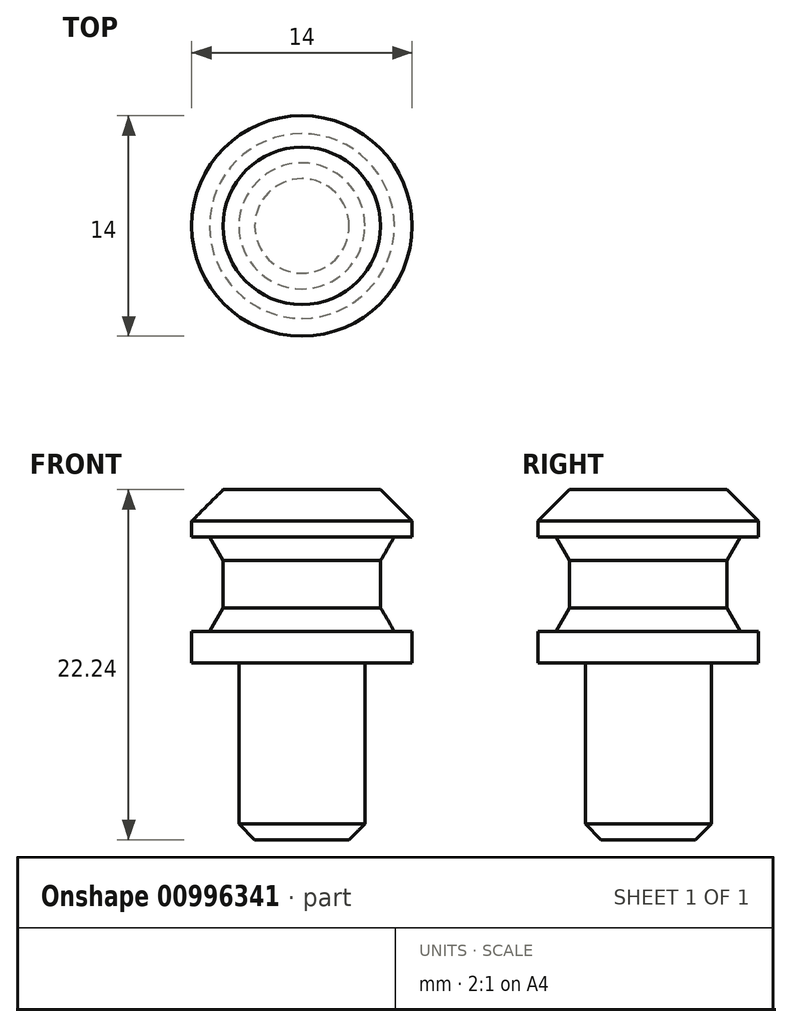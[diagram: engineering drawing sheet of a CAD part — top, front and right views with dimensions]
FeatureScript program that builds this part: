
annotation { "Feature Type Name" : "Feature", "Feature Type Description" : "" }
export const myFeature = defineFeature(function(context is Context, id is Id, definition is map)
    precondition{}
    {
        {
            var Q0;
            Q0=qCreatedBy(makeId("Front.planeOp"),FACE);
            var sketch = newSketch(context, id + "F0", { "sketchPlane" : qUnion([Q0])});
            skLineSegment(sketch, "E0", {"start": v(0, -11.24) * mm, "end": v(4, -11.24) * mm});
            skLineSegment(sketch, "E1", {"start": v(4, -11.24) * mm, "end": v(4, 0) * mm});
            skLineSegment(sketch, "E2", {"start": v(4, 0) * mm, "end": v(7, 0) * mm});
            skLineSegment(sketch, "E3", {"start": v(7, 0) * mm, "end": v(7, 2) * mm});
            skLineSegment(sketch, "E4", {"start": v(7, 2) * mm, "end": v(5.87, 2) * mm});
            skLineSegment(sketch, "E5", {"start": v(5.87, 2) * mm, "end": v(5, 3.5) * mm});
            skLineSegment(sketch, "E6", {"start": v(5, 3.5) * mm, "end": v(5, 6.5) * mm});
            skLineSegment(sketch, "E7", {"start": v(5, 6.5) * mm, "end": v(5.87, 8) * mm});
            skLineSegment(sketch, "E8", {"start": v(5.87, 8) * mm, "end": v(7, 8) * mm});
            skLineSegment(sketch, "E9", {"start": v(7, 8) * mm, "end": v(7, 11) * mm});
            skLineSegment(sketch, "E10", {"start": v(7, 11) * mm, "end": v(0, 11) * mm});
            skLineSegment(sketch, "E11", {"start": v(0, 11) * mm, "end": v(0, -11.24) * mm});
            skSolve(sketch);
        }
        {
            var Q0;
            Q0=makeQuery(id+"F0.imprint","IMPRINT",FACE,{"disambiguationData":[TD([[makeQuery(id+"F0.imprint","IMPRINT",EDGE,{"derivedFrom":sQuery(id+"F0.wireOp",EDGE,"E0")}),1.0]])]});
            var Q1;
            Q1=sQuery(id+"F0.wireOp",EDGE,"E11");
            revolve(context, id + "F1", {"surfaceOperationType" : NewSurfaceOperationType.NEW, "entities" : qUnion([Q0]), "axis" : qUnion([Q1]), "revolveType" : RevolveType.FULL});
        }
        {
            var Q0;
            Q0=makeQuery(id+"F1.opRevolve","SWEPT_EDGE",EDGE,{"disambiguationData":[OSD([sQuery(id+"F0.wireOp",EDGE,"E9"),sQuery(id+"F0.wireOp",EDGE,"E10")])]});
            chamfer(context, id + "F2", {"entities" : qUnion([Q0]), "width" : 2 * mm, "tangentPropagation" : true});
        }
        {
            var Q0;
            Q0=makeQuery(id+"F1.opRevolve","SWEPT_EDGE",EDGE,{"disambiguationData":[OSD([sQuery(id+"F0.wireOp",EDGE,"E0"),sQuery(id+"F0.wireOp",EDGE,"E1")])]});
            chamfer(context, id + "F3", {"entities" : qUnion([Q0]), "width" : 1 * mm, "tangentPropagation" : true});
        }
    });
